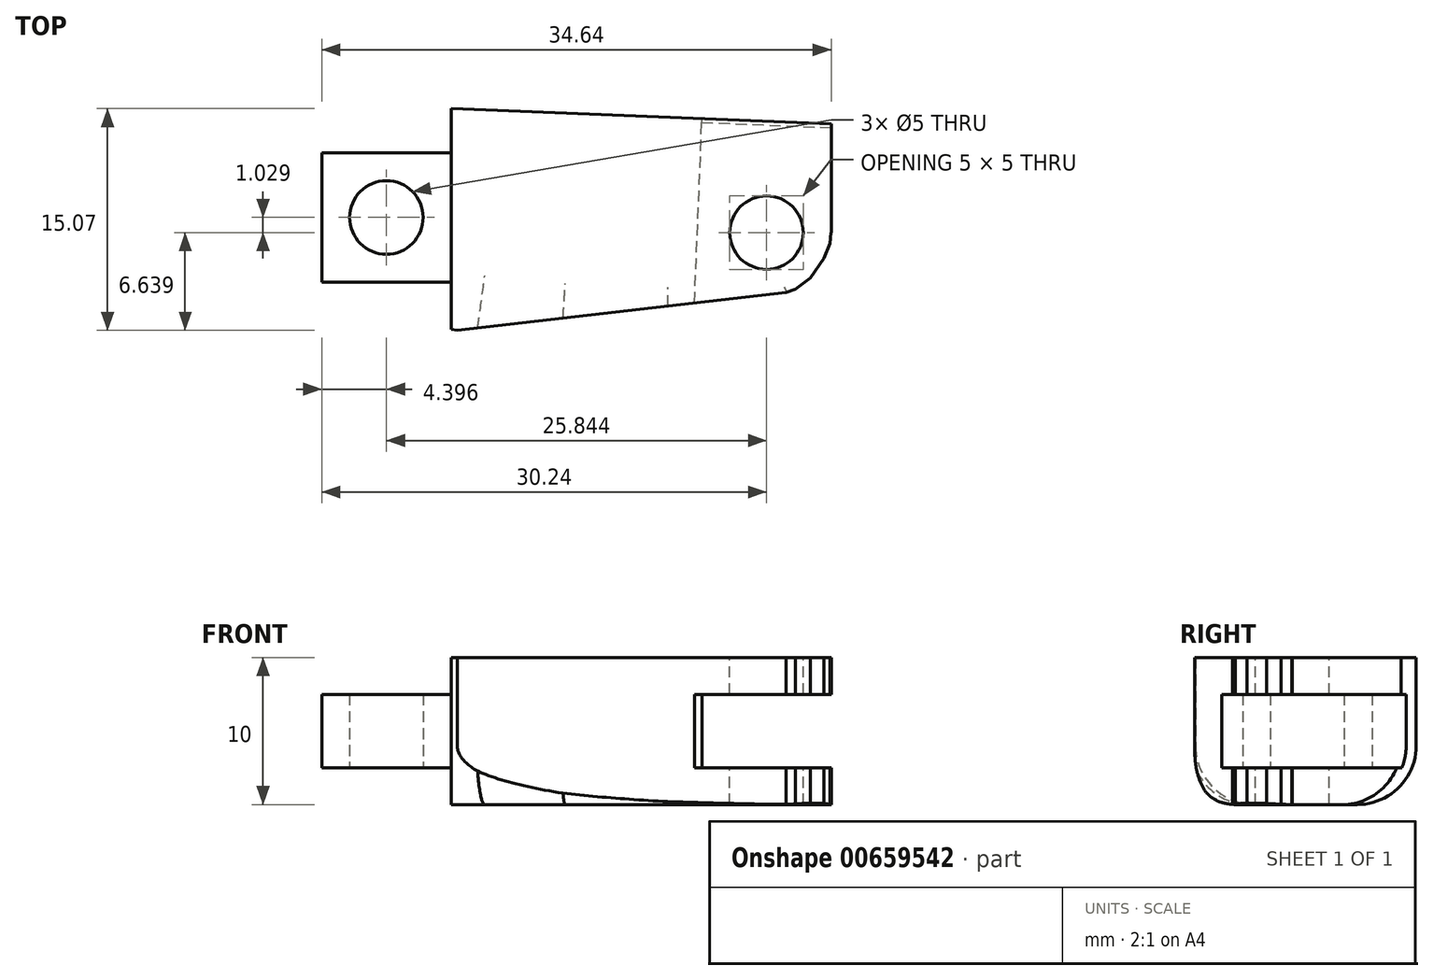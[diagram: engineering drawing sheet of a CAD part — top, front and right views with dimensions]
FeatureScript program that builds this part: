
annotation { "Feature Type Name" : "Feature", "Feature Type Description" : "" }
export const myFeature = defineFeature(function(context is Context, id is Id, definition is map)
    precondition{}
    {
        {
            var Q0;
            Q0=qCreatedBy(makeId("Top.planeOp"),FACE);
            var sketch = newSketch(context, id + "F0", { "sketchPlane" : qUnion([Q0])});
            skLineSegment(sketch, "E0", {"start": v(0, 2) * mm, "end": v(0, 15.13) * mm});
            skLineSegment(sketch, "E1", {"start": v(0, 15.13) * mm, "end": v(-25.84, 16.16) * mm});
            skLineSegment(sketch, "E2", {"start": v(-25.84, 16.16) * mm, "end": v(-25.84, 13.16) * mm});
            skLineSegment(sketch, "E3", {"start": v(0, 2) * mm, "end": v(-0.7, 1.16) * mm});
            skLineSegment(sketch, "E4", {"start": v(-0.7, 1.16) * mm, "end": v(-1.76, 0.53) * mm});
            skLineSegment(sketch, "E5", {"start": v(-1.76, 0.53) * mm, "end": v(-3.9, 0) * mm});
            skLineSegment(sketch, "E6", {"start": v(-3.9, 0) * mm, "end": v(-11.18, 0) * mm});
            skLineSegment(sketch, "E7", {"start": v(-11.18, 0) * mm, "end": v(-18.36, 0.29) * mm});
            skLineSegment(sketch, "E8", {"start": v(-18.36, 0.29) * mm, "end": v(-24.1, 0.85) * mm});
            skLineSegment(sketch, "E9", {"start": v(-24.1, 0.85) * mm, "end": v(-25.84, 1.16) * mm});
            skPoint(sketch, "E10.orphan", {"position": v(-25.84, 0) * mm});
            skPoint(sketch, "E11.orphan", {"position": v(0, 0) * mm});
            skLineSegment(sketch, "E12.bottom", {"start": v(-25.84, 13.16) * mm, "end": v(-34.64, 13.16) * mm});
            skLineSegment(sketch, "E12.top", {"start": v(-25.84, 4.36) * mm, "end": v(-34.64, 4.36) * mm});
            skLineSegment(sketch, "E12.right", {"start": v(-34.64, 13.16) * mm, "end": v(-34.64, 4.36) * mm});
            skLineSegment(sketch, "E13.trimOffspring", {"start": v(-25.84, 4.36) * mm, "end": v(-25.84, 1.16) * mm});
            skCircle(sketch, "E14", {"center": v(-30.24, 8.76) * mm, "radius": 2.5 * mm});
            skPoint(sketch, "E14.centerSnap0", {"position": v(-30.24, 13.16) * mm});
            skPoint(sketch, "E14.centerSnap1", {"position": v(-34.64, 8.76) * mm});
            skSolve(sketch);
        }
        {
            var Q0;
            Q0=makeQuery(id+"F0.imprint","IMPRINT",FACE,{"disambiguationData":[TD([[makeQuery(id+"F0.imprint","IMPRINT",EDGE,{"derivedFrom":sQuery(id+"F0.wireOp",EDGE,"E0")}),1.0]])]});
            extrude(context, id + "F1", {"entities" : qUnion([Q0]), "depth" : 10 * mm, "offsetDistance" : 25 * mm});
        }
        {
            var Q0;
            Q0=makeQuery(id+"F1.opExtrude","SWEPT_FACE",FACE,{"disambiguationData":[OSD([sQuery(id+"F0.wireOp",EDGE,"E0")])]});
            var sketch = newSketch(context, id + "F2", { "sketchPlane" : qUnion([Q0])});
            skLineSegment(sketch, "E15.bottom", {"start": v(3.33, 7.5) * mm, "end": v(12.13, 7.5) * mm});
            skLineSegment(sketch, "E15.top", {"start": v(3.33, 2.5) * mm, "end": v(12.13, 2.5) * mm});
            skLineSegment(sketch, "E15.left", {"start": v(3.33, 7.5) * mm, "end": v(3.33, 2.5) * mm});
            skLineSegment(sketch, "E15.right", {"start": v(12.13, 7.5) * mm, "end": v(12.13, 2.5) * mm});
            skSolve(sketch);
        }
        {
            var Q0;
            Q0=makeQuery(id+"F2.imprint","IMPRINT",FACE,{"disambiguationData":[TD([[makeQuery(id+"F2.imprint","IMPRINT",EDGE,{"derivedFrom":sQuery(id+"F2.wireOp",EDGE,"E15.bottom")}),-1.0]])]});
            extrude(context, id + "F3", {"entities" : qUnion([Q0]), "operationType" : NewBodyOperationType.REMOVE, "oppositeDirection" : true, "depth" : 8.8 * mm, "offsetDistance" : 25 * mm});
        }
        {
            var Q0;
            Q0=makeQuery(id+"F1.opExtrude","CAP_FACE",FACE,{"disambiguationData":[OSD([sQuery(id+"F0.wireOp",EDGE,"E0"),sQuery(id+"F0.wireOp",EDGE,"E1"),sQuery(id+"F0.wireOp",EDGE,"E2"),sQuery(id+"F0.wireOp",EDGE,"E3"),sQuery(id+"F0.wireOp",EDGE,"E4"),sQuery(id+"F0.wireOp",EDGE,"E5"),sQuery(id+"F0.wireOp",EDGE,"E6"),sQuery(id+"F0.wireOp",EDGE,"E7"),sQuery(id+"F0.wireOp",EDGE,"E8"),sQuery(id+"F0.wireOp",EDGE,"E9"),sQuery(id+"F0.wireOp",EDGE,"E12.bottom"),sQuery(id+"F0.wireOp",EDGE,"E12.top"),sQuery(id+"F0.wireOp",EDGE,"E12.right"),sQuery(id+"F0.wireOp",EDGE,"E13.trimOffspring"),sQuery(id+"F0.wireOp",EDGE,"E14")])],"isStart":true});
            var sketch = newSketch(context, id + "F4", { "sketchPlane" : qUnion([Q0])});
            skLineSegment(sketch, "E16", {"start": v(-25.84, -13.16) * mm, "end": v(-25.84, -4.36) * mm});
            skSolve(sketch);
        }
        {
            var Q0;
            Q0=makeQuery(id+"F4.imprint","IMPRINT",FACE,{"disambiguationData":[TD([[makeQuery(id+"F4.imprint","IMPRINT",EDGE,{"derivedFrom":sQuery(id+"F4.wireOp",EDGE,"E16")}),1.0]])]});
            extrude(context, id + "F5", {"entities" : qUnion([Q0]), "operationType" : NewBodyOperationType.REMOVE, "oppositeDirection" : true, "depth" : 2.5 * mm, "offsetDistance" : 25 * mm});
        }
        {
            var Q0;
            Q0=makeQuery(id+"F1.opExtrude","CAP_FACE",FACE,{"disambiguationData":[OSD([sQuery(id+"F0.wireOp",EDGE,"E0"),sQuery(id+"F0.wireOp",EDGE,"E1"),sQuery(id+"F0.wireOp",EDGE,"E2"),sQuery(id+"F0.wireOp",EDGE,"E3"),sQuery(id+"F0.wireOp",EDGE,"E4"),sQuery(id+"F0.wireOp",EDGE,"E5"),sQuery(id+"F0.wireOp",EDGE,"E6"),sQuery(id+"F0.wireOp",EDGE,"E7"),sQuery(id+"F0.wireOp",EDGE,"E8"),sQuery(id+"F0.wireOp",EDGE,"E9"),sQuery(id+"F0.wireOp",EDGE,"E12.bottom"),sQuery(id+"F0.wireOp",EDGE,"E12.top"),sQuery(id+"F0.wireOp",EDGE,"E12.right"),sQuery(id+"F0.wireOp",EDGE,"E13.trimOffspring"),sQuery(id+"F0.wireOp",EDGE,"E14")])],"isStart":false});
            var sketch = newSketch(context, id + "F6", { "sketchPlane" : qUnion([Q0])});
            skLineSegment(sketch, "E17", {"start": v(-25.84, 13.16) * mm, "end": v(-25.84, 4.36) * mm});
            skSolve(sketch);
        }
        {
            var Q0;
            Q0=makeQuery(id+"F6.imprint","IMPRINT",FACE,{"disambiguationData":[TD([[makeQuery(id+"F6.imprint","IMPRINT",EDGE,{"derivedFrom":sQuery(id+"F6.wireOp",EDGE,"E17")}),-1.0]])]});
            extrude(context, id + "F7", {"entities" : qUnion([Q0]), "operationType" : NewBodyOperationType.REMOVE, "oppositeDirection" : true, "depth" : 2.5 * mm, "offsetDistance" : 25 * mm});
        }
        {
            var Q0;
            Q0=makeQuery(id+"F1.opExtrude","CAP_FACE",FACE,{"disambiguationData":[OSD([sQuery(id+"F0.wireOp",EDGE,"E0"),sQuery(id+"F0.wireOp",EDGE,"E1"),sQuery(id+"F0.wireOp",EDGE,"E2"),sQuery(id+"F0.wireOp",EDGE,"E3"),sQuery(id+"F0.wireOp",EDGE,"E4"),sQuery(id+"F0.wireOp",EDGE,"E5"),sQuery(id+"F0.wireOp",EDGE,"E6"),sQuery(id+"F0.wireOp",EDGE,"E7"),sQuery(id+"F0.wireOp",EDGE,"E8"),sQuery(id+"F0.wireOp",EDGE,"E9"),sQuery(id+"F0.wireOp",EDGE,"E12.bottom"),sQuery(id+"F0.wireOp",EDGE,"E12.top"),sQuery(id+"F0.wireOp",EDGE,"E12.right"),sQuery(id+"F0.wireOp",EDGE,"E13.trimOffspring"),sQuery(id+"F0.wireOp",EDGE,"E14")])],"isStart":false});
            var sketch = newSketch(context, id + "F8", { "sketchPlane" : qUnion([Q0])});
            skLineSegment(sketch, "E18.bottom", {"start": v(0, 12.13) * mm, "end": v(-8.8, 12.13) * mm});
            skLineSegment(sketch, "E18.top", {"start": v(0, 3.33) * mm, "end": v(-8.8, 3.33) * mm});
            skLineSegment(sketch, "E18.left", {"start": v(0, 12.13) * mm, "end": v(0, 3.33) * mm});
            skLineSegment(sketch, "E18.right", {"start": v(-8.8, 12.13) * mm, "end": v(-8.8, 3.33) * mm});
            skCircle(sketch, "E19", {"center": v(-4.4, 7.73) * mm, "radius": 2.5 * mm});
            skPoint(sketch, "E19.centerSnap0", {"position": v(-8.8, 7.73) * mm});
            skPoint(sketch, "E19.centerSnap1", {"position": v(-4.4, 12.13) * mm});
            skSolve(sketch);
        }
        {
            var Q0;
            Q0=makeQuery(id+"F8.imprint","IMPRINT",FACE,{"disambiguationData":[TD([[makeQuery(id+"F8.imprint","IMPRINT",EDGE,{"derivedFrom":sQuery(id+"F8.wireOp",EDGE,"E19")}),1.0]])]});
            extrude(context, id + "F9", {"entities" : qUnion([Q0]), "operationType" : NewBodyOperationType.REMOVE, "oppositeDirection" : true, "depth" : 25 * mm, "offsetDistance" : 25 * mm});
        }
        {
            var Q0;
            Q0=makeQuery(id+"F1.opExtrude","SWEPT_FACE",FACE,{"disambiguationData":[OSD([sQuery(id+"F0.wireOp",EDGE,"E1")])]});
            var sketch = newSketch(context, id + "F10", { "sketchPlane" : qUnion([Q0])});
            skLineSegment(sketch, "E20.bottom", {"start": v(0.6, 7.5) * mm, "end": v(9.4, 7.5) * mm});
            skLineSegment(sketch, "E20.top", {"start": v(0.6, 2.5) * mm, "end": v(9.4, 2.5) * mm});
            skLineSegment(sketch, "E20.right", {"start": v(9.4, 7.5) * mm, "end": v(9.4, 2.5) * mm});
            skLineSegment(sketch, "E21", {"start": v(0.6, 7.5) * mm, "end": v(-4.18, 7.5) * mm});
            skLineSegment(sketch, "E22", {"start": v(0.6, 2.5) * mm, "end": v(-4.18, 2.5) * mm});
            skLineSegment(sketch, "E23", {"start": v(-4.18, 2.5) * mm, "end": v(-4.18, 7.5) * mm});
            skSolve(sketch);
        }
        {
            var Q0;
            {var subQ0=sQuery(id+"F10.wireOp",EDGE,"E21");Q0=makeQuery(id+"F10.imprint","IMPRINT",FACE,{"disambiguationData":[TD([[makeQuery(id+"F10.imprint","IMPRINT",EDGE,{"derivedFrom":subQ0}),1.0]])]});}
            var Q1;
            {var subQ0=sQuery(id+"F10.wireOp",EDGE,"E20.bottom");Q1=makeQuery(id+"F10.imprint","IMPRINT",FACE,{"disambiguationData":[TD([[makeQuery(id+"F10.imprint","IMPRINT",EDGE,{"derivedFrom":subQ0}),-1.0]])]});}
            extrude(context, id + "F11", {"entities" : qUnion([Q0, Q1]), "operationType" : NewBodyOperationType.REMOVE, "oppositeDirection" : true, "depth" : 25 * mm, "offsetDistance" : 25 * mm});
        }
        {
            var Q0;
            Q0=makeQuery(id+"F1.opExtrude","CAP_EDGE",EDGE,{"disambiguationData":[OSD([sQuery(id+"F0.wireOp",EDGE,"E8")])],"isStart":true});
            var Q1;
            Q1=makeQuery(id+"F1.opExtrude","CAP_EDGE",EDGE,{"disambiguationData":[OSD([sQuery(id+"F0.wireOp",EDGE,"E6")])],"isStart":true});
            var Q2;
            Q2=makeQuery(id+"F1.opExtrude","CAP_EDGE",EDGE,{"disambiguationData":[OSD([sQuery(id+"F0.wireOp",EDGE,"E9")])],"isStart":true});
            var Q3;
            Q3=makeQuery(id+"F1.opExtrude","CAP_EDGE",EDGE,{"disambiguationData":[OSD([sQuery(id+"F0.wireOp",EDGE,"E3")])],"isStart":true});
            var Q4;
            Q4=makeQuery(id+"F1.opExtrude","CAP_EDGE",EDGE,{"disambiguationData":[OSD([sQuery(id+"F0.wireOp",EDGE,"E1")])],"isStart":true});
            fillet(context, id + "F12", {"entities" : qUnion([Q0, Q1, Q2, Q3, Q4]), "radius" : 4 * mm, "tangentPropagation" : true, "allowEdgeOverflow" : false});
        }
        {
            var Q0;
            Q0=makeQuery(id+"F1.opExtrude","CAP_FACE",FACE,{"disambiguationData":[OSD([sQuery(id+"F0.wireOp",EDGE,"E0"),sQuery(id+"F0.wireOp",EDGE,"E1"),sQuery(id+"F0.wireOp",EDGE,"E2"),sQuery(id+"F0.wireOp",EDGE,"E3"),sQuery(id+"F0.wireOp",EDGE,"E4"),sQuery(id+"F0.wireOp",EDGE,"E5"),sQuery(id+"F0.wireOp",EDGE,"E6"),sQuery(id+"F0.wireOp",EDGE,"E7"),sQuery(id+"F0.wireOp",EDGE,"E8"),sQuery(id+"F0.wireOp",EDGE,"E9"),sQuery(id+"F0.wireOp",EDGE,"E12.bottom"),sQuery(id+"F0.wireOp",EDGE,"E12.top"),sQuery(id+"F0.wireOp",EDGE,"E12.right"),sQuery(id+"F0.wireOp",EDGE,"E13.trimOffspring"),sQuery(id+"F0.wireOp",EDGE,"E14")])],"isStart":true});
            var sketch = newSketch(context, id + "F13", { "sketchPlane" : qUnion([Q0])});
            skArc(sketch, "E24", {"start": v(2.66, -7.95) * mm, "mid": v(-4.98, -1.7) * mm, "end": v(-14.7, 0) * mm});
            skLineSegment(sketch, "E25", {"start": v(2.66, -7.95) * mm, "end": v(6.95, 0.36) * mm});
            skLineSegment(sketch, "E26", {"start": v(6.95, 0.36) * mm, "end": v(-10.89, 3.76) * mm});
            skLineSegment(sketch, "E27", {"start": v(-10.89, 3.76) * mm, "end": v(-14.7, 0) * mm});
            skSolve(sketch);
        }
        {
            var Q0;
            Q0=makeQuery(id+"F13.imprint","IMPRINT",FACE,{"disambiguationData":[TD([[makeQuery(id+"F13.imprint","IMPRINT",EDGE,{"derivedFrom":sQuery(id+"F13.wireOp",EDGE,"E24")}),-1.0]])]});
            extrude(context, id + "F14", {"entities" : qUnion([Q0]), "operationType" : NewBodyOperationType.REMOVE, "oppositeDirection" : true, "depth" : 25 * mm, "offsetDistance" : 25 * mm});
        }
        {
            var Q0;
            Q0=makeQuery(id+"F1.opExtrude","CAP_FACE",FACE,{"disambiguationData":[OSD([sQuery(id+"F0.wireOp",EDGE,"E0"),sQuery(id+"F0.wireOp",EDGE,"E1"),sQuery(id+"F0.wireOp",EDGE,"E2"),sQuery(id+"F0.wireOp",EDGE,"E3"),sQuery(id+"F0.wireOp",EDGE,"E4"),sQuery(id+"F0.wireOp",EDGE,"E5"),sQuery(id+"F0.wireOp",EDGE,"E6"),sQuery(id+"F0.wireOp",EDGE,"E7"),sQuery(id+"F0.wireOp",EDGE,"E8"),sQuery(id+"F0.wireOp",EDGE,"E9"),sQuery(id+"F0.wireOp",EDGE,"E12.bottom"),sQuery(id+"F0.wireOp",EDGE,"E12.top"),sQuery(id+"F0.wireOp",EDGE,"E12.right"),sQuery(id+"F0.wireOp",EDGE,"E13.trimOffspring"),sQuery(id+"F0.wireOp",EDGE,"E14")])],"isStart":true});
            var sketch = newSketch(context, id + "F15", { "sketchPlane" : qUnion([Q0])});
            skArc(sketch, "E28", {"start": v(0.27, -7.73) * mm, "mid": v(-0.44, -5.25) * mm, "end": v(-2.35, -3.53) * mm});
            skLineSegment(sketch, "E29", {"start": v(-1.58, -4) * mm, "end": v(-5.03, -1.88) * mm});
            skLineSegment(sketch, "E30", {"start": v(-5.03, -1.88) * mm, "end": v(-11.15, 0) * mm});
            skLineSegment(sketch, "E31", {"start": v(-11.15, 0) * mm, "end": v(-11.15, 2.12) * mm});
            skLineSegment(sketch, "E32", {"start": v(-11.15, 2.12) * mm, "end": v(3.89, 1.4) * mm});
            skLineSegment(sketch, "E33", {"start": v(3.89, 1.4) * mm, "end": v(3.89, -7.63) * mm});
            skLineSegment(sketch, "E34", {"start": v(3.89, -7.63) * mm, "end": v(0.27, -7.73) * mm});
            skPoint(sketch, "E35.end.orphan", {"position": v(0, -7.73) * mm});
            skSolve(sketch);
        }
        {
            var Q0;
            {var subQ0=sQuery(id+"F15.wireOp",EDGE,"E30");Q0=makeQuery(id+"F15.imprint","IMPRINT",FACE,{"disambiguationData":[TD([[makeQuery(id+"F15.imprint","IMPRINT",EDGE,{"derivedFrom":subQ0}),-1.0]])]});}
            extrude(context, id + "F16", {"entities" : qUnion([Q0]), "operationType" : NewBodyOperationType.REMOVE, "oppositeDirection" : true, "depth" : 25 * mm, "offsetDistance" : 25 * mm});
        }
        {
            var Q0;
            Q0=makeQuery(id+"F1.opExtrude","CAP_FACE",FACE,{"disambiguationData":[OSD([sQuery(id+"F0.wireOp",EDGE,"E0"),sQuery(id+"F0.wireOp",EDGE,"E1"),sQuery(id+"F0.wireOp",EDGE,"E2"),sQuery(id+"F0.wireOp",EDGE,"E3"),sQuery(id+"F0.wireOp",EDGE,"E4"),sQuery(id+"F0.wireOp",EDGE,"E5"),sQuery(id+"F0.wireOp",EDGE,"E6"),sQuery(id+"F0.wireOp",EDGE,"E7"),sQuery(id+"F0.wireOp",EDGE,"E8"),sQuery(id+"F0.wireOp",EDGE,"E9"),sQuery(id+"F0.wireOp",EDGE,"E12.bottom"),sQuery(id+"F0.wireOp",EDGE,"E12.top"),sQuery(id+"F0.wireOp",EDGE,"E12.right"),sQuery(id+"F0.wireOp",EDGE,"E13.trimOffspring"),sQuery(id+"F0.wireOp",EDGE,"E14")])],"isStart":true});
            var sketch = newSketch(context, id + "F17", { "sketchPlane" : qUnion([Q0])});
            skLineSegment(sketch, "E36", {"start": v(0.4, -8.06) * mm, "end": v(-0.38, -5.97) * mm});
            skLineSegment(sketch, "E37", {"start": v(-0.38, -5.97) * mm, "end": v(-1.26, -4.64) * mm});
            skLineSegment(sketch, "E38", {"start": v(-1.26, -4.64) * mm, "end": v(-2.32, -3.8) * mm});
            skLineSegment(sketch, "E39", {"start": v(-2.32, -3.8) * mm, "end": v(-3.77, -2.83) * mm});
            skLineSegment(sketch, "E40", {"start": v(-3.77, -2.83) * mm, "end": v(-7.97, -0.65) * mm});
            skLineSegment(sketch, "E41", {"start": v(-7.97, -0.65) * mm, "end": v(-7.12, 1.68) * mm});
            skLineSegment(sketch, "E42", {"start": v(-7.12, 1.68) * mm, "end": v(2.55, -5.55) * mm});
            skLineSegment(sketch, "E43", {"start": v(2.55, -5.55) * mm, "end": v(0.4, -8.06) * mm});
            skSolve(sketch);
        }
        {
            var Q0;
            Q0=makeQuery(id+"F17.imprint","IMPRINT",FACE,{"disambiguationData":[TD([[makeQuery(id+"F17.imprint","IMPRINT",EDGE,{"derivedFrom":sQuery(id+"F17.wireOp",EDGE,"E36")}),-1.0]])]});
            extrude(context, id + "F18", {"entities" : qUnion([Q0]), "operationType" : NewBodyOperationType.REMOVE, "oppositeDirection" : true, "depth" : 25 * mm, "offsetDistance" : 25 * mm});
        }
        {
            var Q0;
            Q0=makeQuery(id+"F1.opExtrude","CAP_FACE",FACE,{"disambiguationData":[OSD([sQuery(id+"F0.wireOp",EDGE,"E0"),sQuery(id+"F0.wireOp",EDGE,"E1"),sQuery(id+"F0.wireOp",EDGE,"E2"),sQuery(id+"F0.wireOp",EDGE,"E3"),sQuery(id+"F0.wireOp",EDGE,"E4"),sQuery(id+"F0.wireOp",EDGE,"E5"),sQuery(id+"F0.wireOp",EDGE,"E6"),sQuery(id+"F0.wireOp",EDGE,"E7"),sQuery(id+"F0.wireOp",EDGE,"E8"),sQuery(id+"F0.wireOp",EDGE,"E9"),sQuery(id+"F0.wireOp",EDGE,"E12.bottom"),sQuery(id+"F0.wireOp",EDGE,"E12.top"),sQuery(id+"F0.wireOp",EDGE,"E12.right"),sQuery(id+"F0.wireOp",EDGE,"E13.trimOffspring"),sQuery(id+"F0.wireOp",EDGE,"E14")])],"isStart":true});
            var sketch = newSketch(context, id + "F19", { "sketchPlane" : qUnion([Q0])});
            skLineSegment(sketch, "E44", {"start": v(-26.42, -0.97) * mm, "end": v(-1.6, -3.83) * mm});
            skLineSegment(sketch, "E45", {"start": v(-1.6, -3.83) * mm, "end": v(-9.85, 2.6) * mm});
            skLineSegment(sketch, "E46", {"start": v(-9.85, 2.6) * mm, "end": v(-26.2, 0.87) * mm});
            skLineSegment(sketch, "E47", {"start": v(-26.2, 0.87) * mm, "end": v(-26.42, -0.97) * mm});
            skSolve(sketch);
        }
        {
            var Q0;
            Q0=makeQuery(id+"F19.imprint","IMPRINT",FACE,{"disambiguationData":[TD([[makeQuery(id+"F19.imprint","IMPRINT",EDGE,{"derivedFrom":sQuery(id+"F19.wireOp",EDGE,"E44")}),1.0]])]});
            extrude(context, id + "F20", {"entities" : qUnion([Q0]), "operationType" : NewBodyOperationType.REMOVE, "oppositeDirection" : true, "depth" : 25 * mm, "offsetDistance" : 25 * mm});
        }
        {
            var Q0;
            Q0=makeQuery(id+"F1.opExtrude","CAP_FACE",FACE,{"disambiguationData":[OSD([sQuery(id+"F0.wireOp",EDGE,"E0"),sQuery(id+"F0.wireOp",EDGE,"E1"),sQuery(id+"F0.wireOp",EDGE,"E2"),sQuery(id+"F0.wireOp",EDGE,"E3"),sQuery(id+"F0.wireOp",EDGE,"E4"),sQuery(id+"F0.wireOp",EDGE,"E5"),sQuery(id+"F0.wireOp",EDGE,"E6"),sQuery(id+"F0.wireOp",EDGE,"E7"),sQuery(id+"F0.wireOp",EDGE,"E8"),sQuery(id+"F0.wireOp",EDGE,"E9"),sQuery(id+"F0.wireOp",EDGE,"E12.bottom"),sQuery(id+"F0.wireOp",EDGE,"E12.top"),sQuery(id+"F0.wireOp",EDGE,"E12.right"),sQuery(id+"F0.wireOp",EDGE,"E13.trimOffspring"),sQuery(id+"F0.wireOp",EDGE,"E14")])],"isStart":true});
            var sketch = newSketch(context, id + "F21", { "sketchPlane" : qUnion([Q0])});
            skLineSegment(sketch, "E48", {"start": v(-3.71, -3.45) * mm, "end": v(-2.44, -3.87) * mm});
            skLineSegment(sketch, "E49", {"start": v(-2.44, -3.87) * mm, "end": v(-1.41, -4.65) * mm});
            skLineSegment(sketch, "E50", {"start": v(-1.41, -4.65) * mm, "end": v(-0.5, -5.98) * mm});
            skLineSegment(sketch, "E51", {"start": v(-0.5, -5.98) * mm, "end": v(-0.07, -6.99) * mm});
            skLineSegment(sketch, "E52", {"start": v(-0.07, -6.99) * mm, "end": v(0.17, -10.3) * mm});
            skLineSegment(sketch, "E53", {"start": v(0.17, -10.3) * mm, "end": v(1.3, -3.4) * mm});
            skLineSegment(sketch, "E54", {"start": v(1.3, -3.4) * mm, "end": v(-3.73, -3.02) * mm});
            skLineSegment(sketch, "E55", {"start": v(-3.73, -3.02) * mm, "end": v(-3.71, -3.45) * mm});
            skSolve(sketch);
        }
        {
            var Q0;
            Q0=makeQuery(id+"F21.imprint","IMPRINT",FACE,{"disambiguationData":[TD([[makeQuery(id+"F21.imprint","IMPRINT",EDGE,{"derivedFrom":sQuery(id+"F21.wireOp",EDGE,"E48")}),1.0]])]});
            extrude(context, id + "F22", {"entities" : qUnion([Q0]), "operationType" : NewBodyOperationType.REMOVE, "oppositeDirection" : true, "depth" : 25 * mm, "offsetDistance" : 25 * mm});
        }
    });
